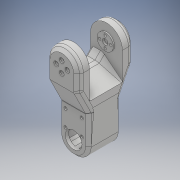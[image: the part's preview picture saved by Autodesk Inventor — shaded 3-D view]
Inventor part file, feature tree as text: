
AUTODESK INVENTOR PART (.ipt)
format: ipt  version: 2018 (Build 220112000, 112)  size: 1,066,496 bytes
history: native  units: mm
features: projected_geometry x42, sketch x40, extrude x33, fillet x13, chamfer x11, hole x8, other x4, mirror x1, reference x1
ambient origin geometry x8: Origin, YZ Plane, XZ Plane, XY Plane, X Axis, Y Axis, Z Axis, Center Point
bodies: Solid1 (feature_tree)
feature tree (153):
  extrude  "Extrusion1"  Depth=45.0mm
  extrude  "Extrusion2"  Depth=2.25mm
  hole  "Hole1"  [1 undecoded]
  hole  "Hole2"  [1 undecoded]
  fillet  "Fillet1"  Radius=14.0mm
  extrude  "Extrusion3"  Depth=18.5mm
  extrude  "Extrusion4"  Depth=10.0mm
  extrude  "Extrusion5"  Depth=2.0mm
  extrude  "Extrusion6"  Depth=2.0mm
  hole  "Hole3"  [1 undecoded]
  extrude  "Extrusion7"  Depth=0.5mm
  extrude  "Extrusion8"  Depth=5.0mm TaperAngle=0.0deg
  extrude  "Extrusion9"  Depth=10.0mm
  extrude  "Extrusion10"  Depth=10.0mm
  extrude  "Extrusion11"  Depth=14.5mm
  extrude  "Extrusion12"  Depth=20.0mm
  extrude  "Extrusion13"  Depth=5.0mm
  extrude  "Extrusion14"  Depth=5.0mm
  extrude  "Extrusion15"  Depth=5.0mm
  extrude  "Extrusion16"  Depth=5.0mm
  extrude  "Extrusion17"  Depth=1.0mm
  chamfer  "Chamfer1"  Distance=1.0mm
  fillet  "Fillet7"  Radius=20.7mm
  fillet  "Fillet8"  Radius=32.0mm
  mirror  "Mirror1"
  extrude  "Extrusion19"  Depth=1.0mm TaperAngle=0.0deg
  extrude  "Extrusion20"  Depth=8.0mm
  extrude  "Extrusion21"  Depth=0.2mm TaperAngle=0.0deg
  extrude  "Extrusion22"  Depth=0.5mm TaperAngle=0.0deg
  extrude  "Extrusion23"  Depth=9.0mm TaperAngle=0.0deg
  extrude  "Extrusion24"  Depth=2.0mm TaperAngle=0.0deg
  chamfer  "Chamfer2"  Distance=0.2mm
  chamfer  "Chamfer8"  Distance=2.0mm Angle=45.0deg
  extrude  "Extrusion25"  Depth=0.5mm
  extrude  "Extrusion26"  Depth=2.0mm TaperAngle=0.0deg
  chamfer  "Chamfer3"  Distance=2.0mm
  chamfer  "Chamfer4"  Distance=2.0mm
  chamfer  "Chamfer5"  Distance=15.0mm
  chamfer  "Chamfer6"  Distance=56.1mm
  fillet  "Fillet9"  Radius=41.6mm
  fillet  "Fillet10"  Radius=41.0mm
  hole  "Hole6"  [1 undecoded]
  fillet  "Fillet12"  Radius=7.0mm
  hole  "Hole7"  [1 undecoded]
  extrude  "Extrusion27"  Depth=3.0mm TaperAngle=45.0deg
  extrude  "Extrusion28"  Depth=5.0mm TaperAngle=45.0deg
  hole  "Hole8"  [1 undecoded]
  extrude  "Extrusion29"  Depth=2.0mm
  chamfer  "Chamfer7"  Distance=1.0mm
  fillet  "Fillet13"  Radius=20.5mm
  extrude  "Extrusion30"  Depth=1.0mm TaperAngle=0.0deg
  extrude  "Extrusion31"  Depth=1.0mm
  fillet  "Fillet14"  Radius=3.1mm
  extrude  "Extrusion32"  Depth=14.0mm
  fillet  "Fillet15"  Radius=16.0mm
  fillet  "Fillet18"  Radius=3.1mm
  extrude  "Extrusion35"  Depth=2.0mm TaperAngle=45.0deg
  extrude  "Extrusion36"  Depth=1.0mm
  chamfer  "Chamfer9"  Distance=37.0mm
  chamfer  "Chamfer10"  Distance=10.0mm
  chamfer  "Chamfer11"  Distance=7.5mm
  fillet  "Fillet19"  Radius=6.0mm
  hole  "Hole9"  [1 undecoded]
  fillet  "Fillet20"  Radius=6.0mm
  hole  "Hole10"  [1 undecoded]
  fillet  "Fillet21"  Radius=3.0mm
  sketch  "Sketch1"  dims[d0=24.5mm d1=45.0mm]
  sketch  "Sketch2"  dims[d2=1.95mm d3=0.0mm d4=2.25mm]
  projected_geometry  "Projected Loop1"
  sketch  "Sketch3"  dims[d5=20.0mm d6=2.25mm]
  projected_geometry  "Projected Loop2"
  sketch  "Sketch4"  dims[d7=5.25mm d8=5.25mm d9=14.0mm]
  projected_geometry  "Projected Loop3"
  sketch  "Sketch5"  dims[d10=5.25mm d11=18.5mm]
  projected_geometry  "Projected Loop4"
  sketch  "Sketch6"  dims[d12=10.0mm d13=0.0mm d14=20.5mm]
  projected_geometry  "Projected Loop5"
  sketch  "Sketch7"  dims[d15=2.0mm d16=2.195mm]
  projected_geometry  "Projected Loop6"
  sketch  "Sketch8"  dims[d17=2.0mm]
  projected_geometry  "Projected Loop7"
  sketch  "Sketch9"  dims[d18=2.4mm d19=6.0mm d20=4.4mm d21=2.0mm d22=90.0deg d23=8.0mm d24=20.594885mm d25=20.5mm]
  projected_geometry  "Projected Loop8"
  projected_geometry  "Projected Loop9"
  sketch  "Sketch10"  dims[d26=26.65mm d27=2.0mm]
  projected_geometry  "Projected Loop10"
  projected_geometry  "Projected Loop11"
  sketch  "Sketch11"  dims[d28=2.0mm]
  projected_geometry  "Projected Loop12"
  sketch  "Sketch12"  dims[d29=2.4mm d30=6.0mm d31=4.4mm d32=2.0mm d33=90.0deg d34=8.0mm d35=20.594885mm d36=0.5mm]
  sketch  "Sketch13"  dims[d37=18.0mm d38=5.0mm d39=0.0mm]
  sketch  "Sketch14"  dims[d41=10.0mm d42=0.0mm d43=24.5mm]
  projected_geometry  "Projected Loop13"
  sketch  "Sketch15"  dims[d44=1.15mm d45=0.0mm d46=10.0mm]
  sketch  "Sketch16"  dims[d47=21.0mm d48=14.5mm]
  projected_geometry  "Projected Loop14"
  sketch  "Sketch17"  dims[d49=20.0mm d50=14.5mm]
  projected_geometry  "Projected Loop15"
  sketch  "Sketch18"  dims[d51=24.5mm d52=5.0mm]
  projected_geometry  "Projected Loop16"
  sketch  "Sketch19"  dims[d53=5.0mm d54=2.25mm]
  projected_geometry  "Projected Loop17"
  sketch  "Sketch20"  dims[d55=2.25mm d56=5.0mm]
  projected_geometry  "Projected Loop18"
  sketch  "Sketch25"  dims[d57=5.0mm d58=9.0mm]
  projected_geometry  "Projected Loop22"
  sketch  "Sketch26"  dims[d59=14.75mm d60=4.0mm d61=1.0mm d62=0.0mm d63=20.7mm]
  projected_geometry  "Projected Loop23"
  sketch  "Sketch27"  dims[d64=2.4mm d65=6.0mm d66=4.4mm d67=2.0mm d68=90.0deg d69=8.0mm d70=20.594885mm d72=32.0mm]
  projected_geometry  "Projected Loop24"
  sketch  "Sketch28"  dims[d73=5.0mm d74=0.0mm d75=1.0mm d76=0.0mm]
  projected_geometry  "Projected Loop25"
  sketch  "Sketch29"  dims[d77=12.25mm d78=0.0mm d80=8.0mm]
  projected_geometry  "Projected Loop26"
  sketch  "Sketch30"  dims[d81=4.5mm d82=0.0mm d84=0.2mm d85=0.0mm]
  projected_geometry  "Projected Loop27"
  sketch  "Sketch31"  dims[d86=21.0mm d87=0.5mm d88=0.0mm]
  sketch  "Sketch33"  dims[d91=8.0mm d92=0.0mm d93=9.0mm d94=0.0mm]
  projected_geometry  "Projected Loop28"
  projected_geometry  "Projected Loop29"
  projected_geometry  "Projected Loop30"
  sketch  "Sketch34"  dims[d95=5.0mm d96=0.0mm d98=0.2mm d99=0.0mm d100=0.2mm d101=0.0mm d102=2.5mm d103=2.0mm d104=45.0deg]
  projected_geometry  "Projected Loop31"
  projected_geometry  "Projected Loop32"
  sketch  "Sketch35"  dims[d105=1.5mm d114=0.5mm]
  projected_geometry  "Projected Loop33"
  sketch  "Sketch36"  dims[d128=2.0mm d129=0.0mm d130=2.0mm d131=0.0mm]
  projected_geometry  "Projected Loop34"
  sketch  "Sketch37"  dims[d132=40.0mm d133=2.0mm d134=0.0mm d135=2.0mm d136=0.0mm]
  projected_geometry  "Projected Loop35"
  sketch  "Sketch38"  dims[d137=40.0mm]
  projected_geometry  "Projected Loop36"
  sketch  "Sketch39"  dims[d138=70.0mm d139=15.0mm d140=0.0mm d141=56.1mm d142=0.0mm]
  projected_geometry  "Projected Loop37"
  sketch  "Sketch40"  dims[d143=4.0mm d144=8.0mm d145=45.0deg d146=41.6mm d147=41.0mm]
  projected_geometry  "Projected Loop38"
  sketch  "Sketch41"  dims[d148=7.0mm d149=7.0mm d150=7.0mm]
  projected_geometry  "Projected Loop39"
  reference  "Reference1"
  sketch  "Sketch44"  dims[d151=100.0mm d152=0.0mm d153=15.282752mm]
  projected_geometry  "Projected Loop42"
  sketch  "Sketch45"  dims[d156=100.0mm d157=0.0mm d158=3.0mm d159=2.0mm d160=45.0deg]
  projected_geometry  "Projected Loop43"
  sketch  "Sketch46"  dims[d161=5.0mm d162=2.0mm d163=45.0deg d164=5.0mm d165=2.0mm d166=45.0deg]
  projected_geometry  "Projected Loop44"
  sketch  "Sketch47"  dims[d167=5.0mm d168=2.0mm d169=45.0deg d170=5.0mm d171=2.0mm d173=5.7mm d174=6.0mm d175=4.0mm d176=2.0mm d177=90.0deg d178=25.0mm d179=0.0mm d180=1.0mm d181=2.459mm d182=25.0mm d183=4.0mm d184=2.0mm d185=90.0deg d186=25.0mm d187=20.594885mm d188=20.5mm d189=1.6mm d190=0.0mm d191=20.5mm d192=3.1mm d193=0.0mm d194=14.0mm d195=3.2mm d196=25.0mm d197=6.3mm d198=2.0mm d199=90.0deg d200=25.0mm d201=20.594885mm d202=16.0mm d203=3.1mm d204=0.0mm d205=1.5mm d206=2.0mm d207=45.0deg d208=1.7mm d209=37.0mm d210=10.0mm d211=0.0mm d212=7.5mm d213=6.0mm d214=6.0mm d215=6.0mm d216=6.0mm d217=3.0mm d218=0.0mm d219=1.5mm d220=6.0mm d221=6.0mm d222=6.0mm d223=6.0mm d224=3.0mm d225=0.0mm d226=1.5mm d231=4.0mm d232=8.0mm d233=45.0deg d234=10.0mm d237=7.0mm d238=2.5mm d239=0.0mm d240=7.0mm d241=2.5mm d242=0.0mm d243=14.0mm d244=25.0mm d245=45.0deg d246=14.0mm d247=25.0mm d248=45.0deg d249=14.0mm d250=25.0mm d251=45.0deg d252=10.0mm d253=4.0mm d254=6.0mm d255=4.0mm d256=2.0mm d257=90.0deg d258=2.0mm d259=20.594885mm d260=1.0mm d261=4.0mm d262=6.0mm d263=4.0mm d264=2.0mm d265=90.0deg d266=2.0mm d267=20.594885mm d268=1.0mm]
  projected_geometry  "Projected Loop45"
  projected_geometry  "Project Cut Edges1"
  projected_geometry  "Project Cut Edges2"
  parser-record x1  (decoder bookkeeping rows leaked as tree rows — omitted from the tree; the rows remain in map.json)
  other  "servocheck.iam"
  other  "bottomarm:1"
  other  "arm1:1"
note: 8 required parameter values undecoded (feature->parameter linkage not recoverable at this tier; creation-order binding heuristic only, values carry confidence <= 0.55)
note: 1 file-system path scrubbed to <path> (originals preserved in map.json)
